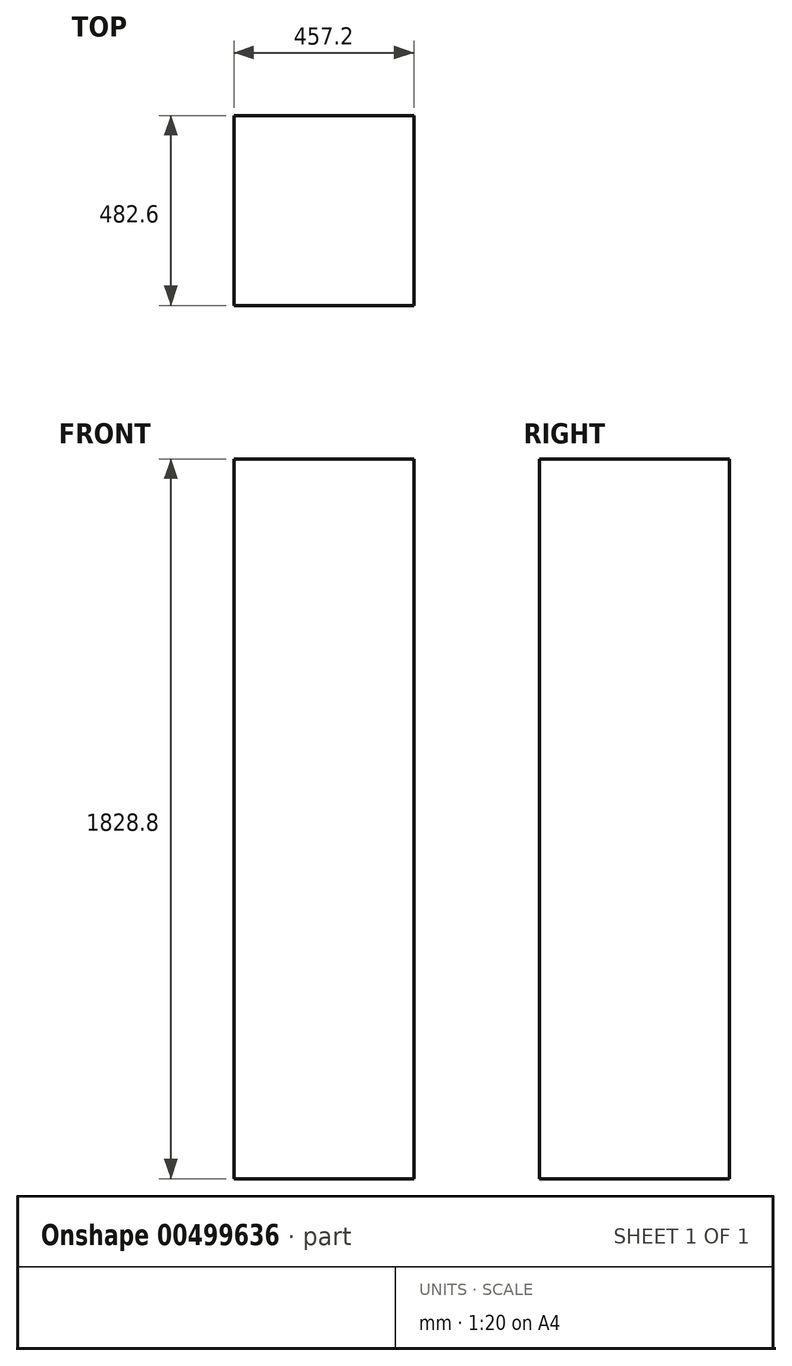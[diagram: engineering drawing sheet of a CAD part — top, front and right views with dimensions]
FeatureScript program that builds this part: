
annotation { "Feature Type Name" : "Feature", "Feature Type Description" : "" }
export const myFeature = defineFeature(function(context is Context, id is Id, definition is map)
    precondition{}
    {
        {
            var Q0;
            Q0=qCreatedBy(makeId("Front.planeOp"),FACE);
            var sketch = newSketch(context, id + "F0", { "sketchPlane" : qUnion([Q0])});
            skLineSegment(sketch, "E0", {"start": v(-59.83, 922.66) * mm, "end": v(-59.83, -906.14) * mm});
            skLineSegment(sketch, "E1", {"start": v(-59.83, 922.66) * mm, "end": v(397.37, 922.66) * mm});
            skLineSegment(sketch, "E2", {"start": v(397.37, 922.66) * mm, "end": v(397.37, -906.14) * mm});
            skLineSegment(sketch, "E3", {"start": v(397.37, -906.14) * mm, "end": v(-59.83, -906.14) * mm});
            skSolve(sketch);
        }
        {
            var Q0;
            Q0=makeQuery(id+"F0.imprint","IMPRINT",FACE,{"disambiguationData":[TD([[makeQuery(id+"F0.imprint","IMPRINT",EDGE,{"derivedFrom":sQuery(id+"F0.wireOp",EDGE,"E0")}),1.0]])]});
            extrude(context, id + "F1", {"entities" : qUnion([Q0]), "depth" : 457.2 * mm});
        }
        {
            var Q0;
            Q0=makeQuery(id+"F1.opExtrude","CAP_FACE",FACE,{"disambiguationData":[OSD([sQuery(id+"F0.wireOp",EDGE,"E0"),sQuery(id+"F0.wireOp",EDGE,"E1"),sQuery(id+"F0.wireOp",EDGE,"E2"),sQuery(id+"F0.wireOp",EDGE,"E3")])],"isStart":false});
            var sketch = newSketch(context, id + "F2", { "sketchPlane" : qUnion([Q0])});
            skLineSegment(sketch, "E4", {"start": v(0, 874.95) * mm, "end": v(0, 617.2) * mm});
            skLineSegment(sketch, "E5", {"start": v(0, 874.95) * mm, "end": v(336.97, 874.95) * mm});
            skLineSegment(sketch, "E6", {"start": v(336.97, 874.95) * mm, "end": v(336.97, 617.2) * mm});
            skLineSegment(sketch, "E7", {"start": v(0, 617.2) * mm, "end": v(336.97, 617.2) * mm});
            skLineSegment(sketch, "E8", {"start": v(168.48, 874.95) * mm, "end": v(168.48, 617.2) * mm});
            skSolve(sketch);
        }
        {
            var Q0;
            {var subQ0=sQuery(id+"F2.wireOp",EDGE,"E6");Q0=makeQuery(id+"F2.imprint","IMPRINT",FACE,{"disambiguationData":[TD([[makeQuery(id+"F2.imprint","IMPRINT",EDGE,{"derivedFrom":subQ0}),-1.0]])]});}
            extrude(context, id + "F3", {"entities" : qUnion([Q0]), "operationType" : NewBodyOperationType.ADD, "oppositeDirection" : true, "depth" : 355.6 * mm});
        }
        {
            var Q0;
            Q0=makeQuery(id+"F1.opExtrude","CAP_FACE",FACE,{"disambiguationData":[OSD([sQuery(id+"F0.wireOp",EDGE,"E0"),sQuery(id+"F0.wireOp",EDGE,"E1"),sQuery(id+"F0.wireOp",EDGE,"E2"),sQuery(id+"F0.wireOp",EDGE,"E3")])],"isStart":false});
            extrude(context, id + "F4", {"entities" : qUnion([Q0]), "operationType" : NewBodyOperationType.ADD, "depth" : 25.4 * mm});
        }
    });
